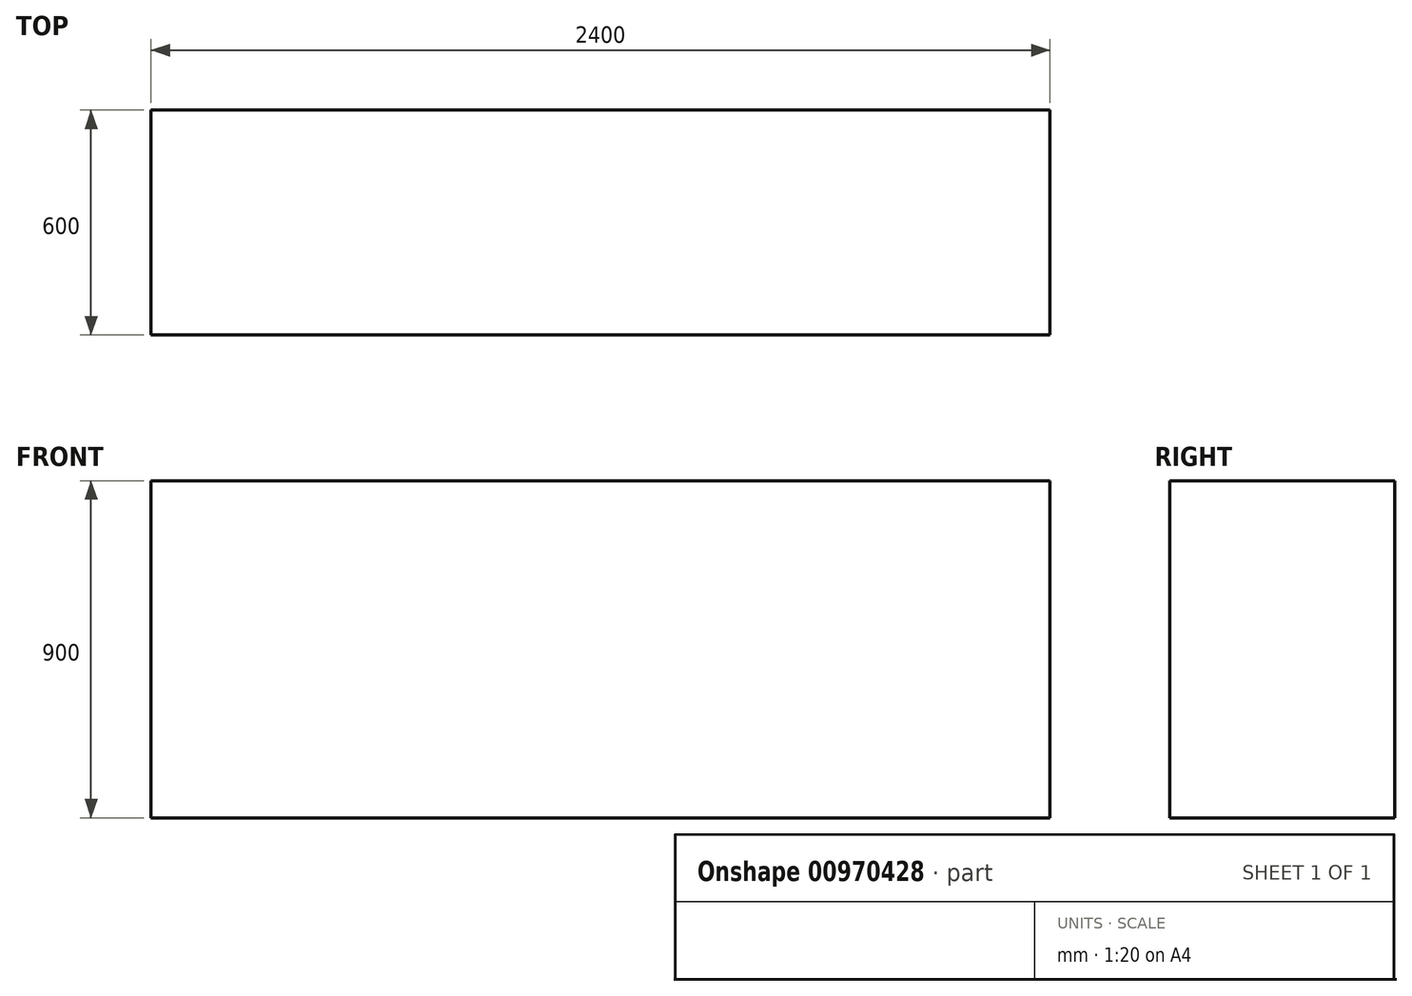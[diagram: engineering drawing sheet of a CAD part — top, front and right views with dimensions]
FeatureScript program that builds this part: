
annotation { "Feature Type Name" : "Feature", "Feature Type Description" : "" }
export const myFeature = defineFeature(function(context is Context, id is Id, definition is map)
    precondition{}
    {
        {
            var Q0;
            Q0=qCreatedBy(makeId("Top.planeOp"),FACE);
            var sketch = newSketch(context, id + "F0", { "sketchPlane" : qUnion([Q0])});
            skLineSegment(sketch, "E0.bottom", {"start": v(-57.38, 553.27) * mm, "end": v(2342.62, 553.27) * mm});
            skLineSegment(sketch, "E0.top", {"start": v(-57.38, -46.73) * mm, "end": v(2342.62, -46.73) * mm});
            skLineSegment(sketch, "E0.left", {"start": v(-57.38, 553.27) * mm, "end": v(-57.38, -46.73) * mm});
            skLineSegment(sketch, "E0.right", {"start": v(2342.62, 553.27) * mm, "end": v(2342.62, -46.73) * mm});
            skSolve(sketch);
        }
        {
            var Q0;
            Q0=makeQuery(id+"F0.imprint","IMPRINT",FACE,{"disambiguationData":[TD([[makeQuery(id+"F0.imprint","IMPRINT",EDGE,{"derivedFrom":sQuery(id+"F0.wireOp",EDGE,"E0.bottom")}),-1.0]])]});
            extrude(context, id + "F1", {"entities" : qUnion([Q0]), "depth" : 900 * mm, "offsetDistance" : 25 * mm});
        }
    });
